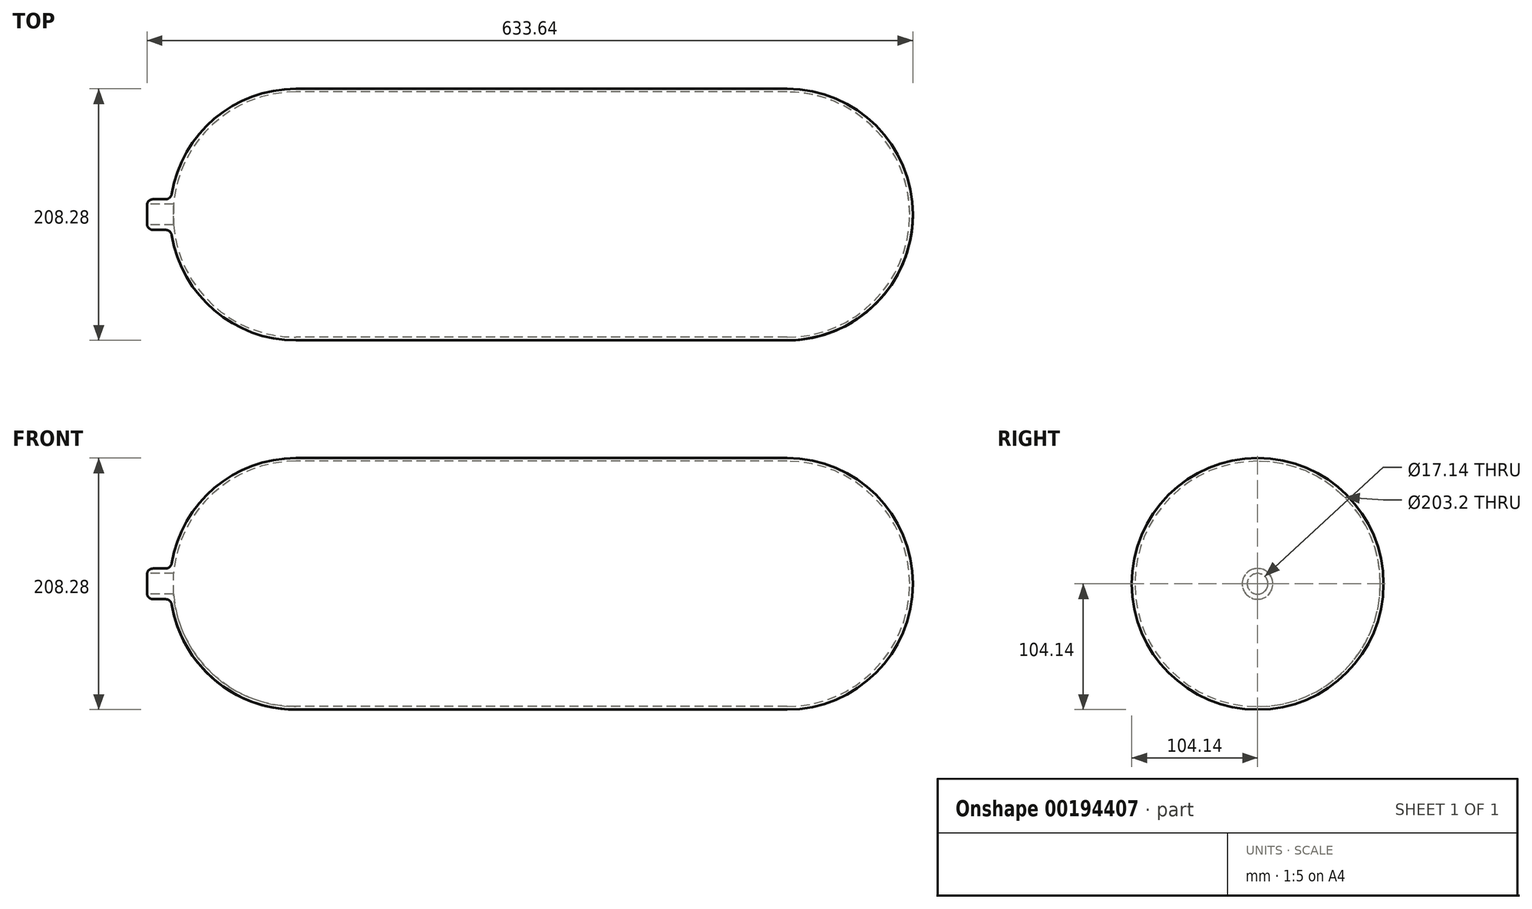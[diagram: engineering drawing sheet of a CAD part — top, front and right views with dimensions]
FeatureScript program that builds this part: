
annotation { "Feature Type Name" : "Feature", "Feature Type Description" : "" }
export const myFeature = defineFeature(function(context is Context, id is Id, definition is map)
    precondition{}
    {
        {
            var Q0;
            Q0=qCreatedBy(makeId("Top.planeOp"),FACE);
            var sketch = newSketch(context, id + "F0", { "sketchPlane" : qUnion([Q0])});
            skLineSegment(sketch, "E0", {"start": v(-198.3, 101.6) * mm, "end": v(208.1, 101.6) * mm});
            skLineSegment(sketch, "E1", {"start": v(-198.3, 0) * mm, "end": v(-299.9, 0) * mm});
            skLineSegment(sketch, "E2", {"start": v(208.1, 0) * mm, "end": v(309.7, 0) * mm});
            skArc(sketch, "E3", {"start": v(-198.3, 101.6) * mm, "mid": v(-270.14, 71.84) * mm, "end": v(-299.9, 0) * mm});
            skArc(sketch, "E4", {"start": v(309.7, 0) * mm, "mid": v(279.94, 71.84) * mm, "end": v(208.1, 101.6) * mm});
            skArc(sketch, "E5.0", {"start": v(312.24, 0) * mm, "mid": v(281.74, 73.64) * mm, "end": v(208.1, 104.14) * mm});
            skLineSegment(sketch, "E5.1", {"start": v(-198.3, 104.14) * mm, "end": v(208.1, 104.14) * mm});
            skArc(sketch, "E5.2", {"start": v(-198.3, 104.14) * mm, "mid": v(-267.3, 78) * mm, "end": v(-301.66, 12.7) * mm});
            skLineSegment(sketch, "E6", {"start": v(-299.9, 0) * mm, "end": v(-302.44, 0) * mm});
            skLineSegment(sketch, "E7", {"start": v(-302.44, 0) * mm, "end": v(-321.49, 0) * mm});
            skLineSegment(sketch, "E8", {"start": v(-321.49, 0) * mm, "end": v(-321.49, 12.7) * mm});
            skLineSegment(sketch, "E9", {"start": v(-321.49, 12.7) * mm, "end": v(-301.66, 12.7) * mm});
            skLineSegment(sketch, "E10", {"start": v(309.7, 0) * mm, "end": v(312.24, 0) * mm});
            skSolve(sketch);
        }
        {
            var Q0;
            Q0=makeQuery(id+"F0.imprint","IMPRINT",FACE,{"disambiguationData":[TD([[makeQuery(id+"F0.imprint","IMPRINT",EDGE,{"derivedFrom":sQuery(id+"F0.wireOp",EDGE,"E0")}),1.0]])]});
            var Q1;
            Q1=sQuery(id+"F0.wireOp",EDGE,"E2");
            revolve(context, id + "F1", {"entities" : qUnion([Q0]), "axis" : qUnion([Q1]), "revolveType" : RevolveType.FULL});
        }
        {
            var Q0;
            Q0=makeQuery(id+"F1.opRevolve","SWEPT_FACE",FACE,{"disambiguationData":[OSD([sQuery(id+"F0.wireOp",EDGE,"E8")])]});
            var sketch = newSketch(context, id + "F2", { "sketchPlane" : qUnion([Q0])});
            skCircle(sketch, "E11", {"center": v(0, 0) * mm, "radius": 8.57 * mm});
            skSolve(sketch);
        }
        {
            var Q0;
            Q0=makeQuery(id+"F1.opRevolve","SWEPT_EDGE",EDGE,{"disambiguationData":[OSD([sQuery(id+"F0.wireOp",EDGE,"E8"),sQuery(id+"F0.wireOp",EDGE,"E9")])]});
            fillet(context, id + "F3", {"entities" : qUnion([Q0]), "radius" : 5.08 * mm, "tangentPropagation" : true, "allowEdgeOverflow" : false});
        }
        {
            var Q0;
            Q0=makeQuery(id+"F1.opRevolve","SWEPT_EDGE",EDGE,{"disambiguationData":[OSD([sQuery(id+"F0.wireOp",EDGE,"E5.2"),sQuery(id+"F0.wireOp",EDGE,"E9")])]});
            fillet(context, id + "F4", {"entities" : qUnion([Q0]), "radius" : 5.08 * mm, "tangentPropagation" : true, "allowEdgeOverflow" : false});
        }
        {
            var Q0;
            Q0=makeQuery(id+"F2.imprint","IMPRINT",FACE,{"disambiguationData":[TD([[makeQuery(id+"F2.imprint","IMPRINT",EDGE,{"derivedFrom":sQuery(id+"F2.wireOp",EDGE,"E11")}),1.0]])]});
            extrude(context, id + "F5", {"entities" : qUnion([Q0]), "operationType" : NewBodyOperationType.REMOVE, "oppositeDirection" : true, "depth" : 25.4 * mm});
        }
    });
